# Revit family: Electronics_Community-Subwoofers_Biamp_VLF_208LV__
name_source: partatom
category: Communication Devices
units: mm (PartAtom-declared; Revit-internal decimal feet)

## family parameters
Cut with Voids When Loaded = No
Host = Face
Maintain Annotation Orientation = No
OmniClass Number = 23.85.10.11.14.14.14
OmniClass Title = Loudspeakers
Part Type = Normal
Room Calculation Point = No
Round Connector Dimension = Use Diameter
Shared = No

## types (2) — shared parameters
Axial Q / DI = 1/0, 40 Hz to 200 Hz
Connector Description = NL4, Terminal strip; 400W continuous, 1000W program, 4 ohms 40 volts RMS, 89 volts momentary peak
Default Elevation = 4' - 0"
Depth = 1' - 9 3/4"
Description = VLF208LV Versatile Low Frequency Dual 8-Inch Large Volume Compact Subwoofer
Drivers = LF (2) 8 inches
Enclosure = 11-ply cross-laminated birch
Height = 0' - 10 3/16"
Input Connection = (2) NL4-compatible locking connector, (1) 2 conductor barrier strip
Loudspeaker Type = Compact, direct-radiating subwoofer
Manufacturer = Biamp
Maximum Output = 119 dB SPL / 126 dB SPL (peak)
Minimum Impedance = 3.9 ohms @ 160 Hz
Mounting/Rigging Provisions = (12) M10 hang points
Nominal Impedance = 4 ohms
Nominal –6dB Beamwidth = 360° H x 180° V
Operating Range = 30 Hz to 1000 Hz, 40 Hz to 200 Hz (±3 dB)
Optional Accessories = VLF-SAB steered array bracket, M10EYBLTKIT 10mm eyebolt kit, STKIT seat track kit
Product Documentation Link = https://downloads.biamp.com
Product Page URL = https://www.biamp.com
Product data url = https://www.bimobject.com
Recommended Power Amplifier = 630W to 900W @ 4 ohms
Recommended Signal Processing = 40 Hz, 24 dB high pass filter
Sensitivity (1W/1m) = 93 dB SPL (40 Hz to 200 Hz 1/3 octave bands)
URL = https://www.biamp.com
Weight = 48.00 lbf
Width = 1' - 9 3/4"

## per-type parameters (varying)
| type | Grill Material | Housing Material | Material of U-bracket |
| VLF208LV B | Biamp - Plastic - Black(Grid) | Biamp - Plastic - Black | Biamp - Metal - Black |
| VLF208LV W | Biamp - Plastic - White(Grid) | Biamp - Plastic - White | Biamp - Metal - White |

note: column(s) folded — value = type name in every type: Model

## geometry (parser evidence)
native form markers: Sweep x6
no freeform markers — native parametric forms only
